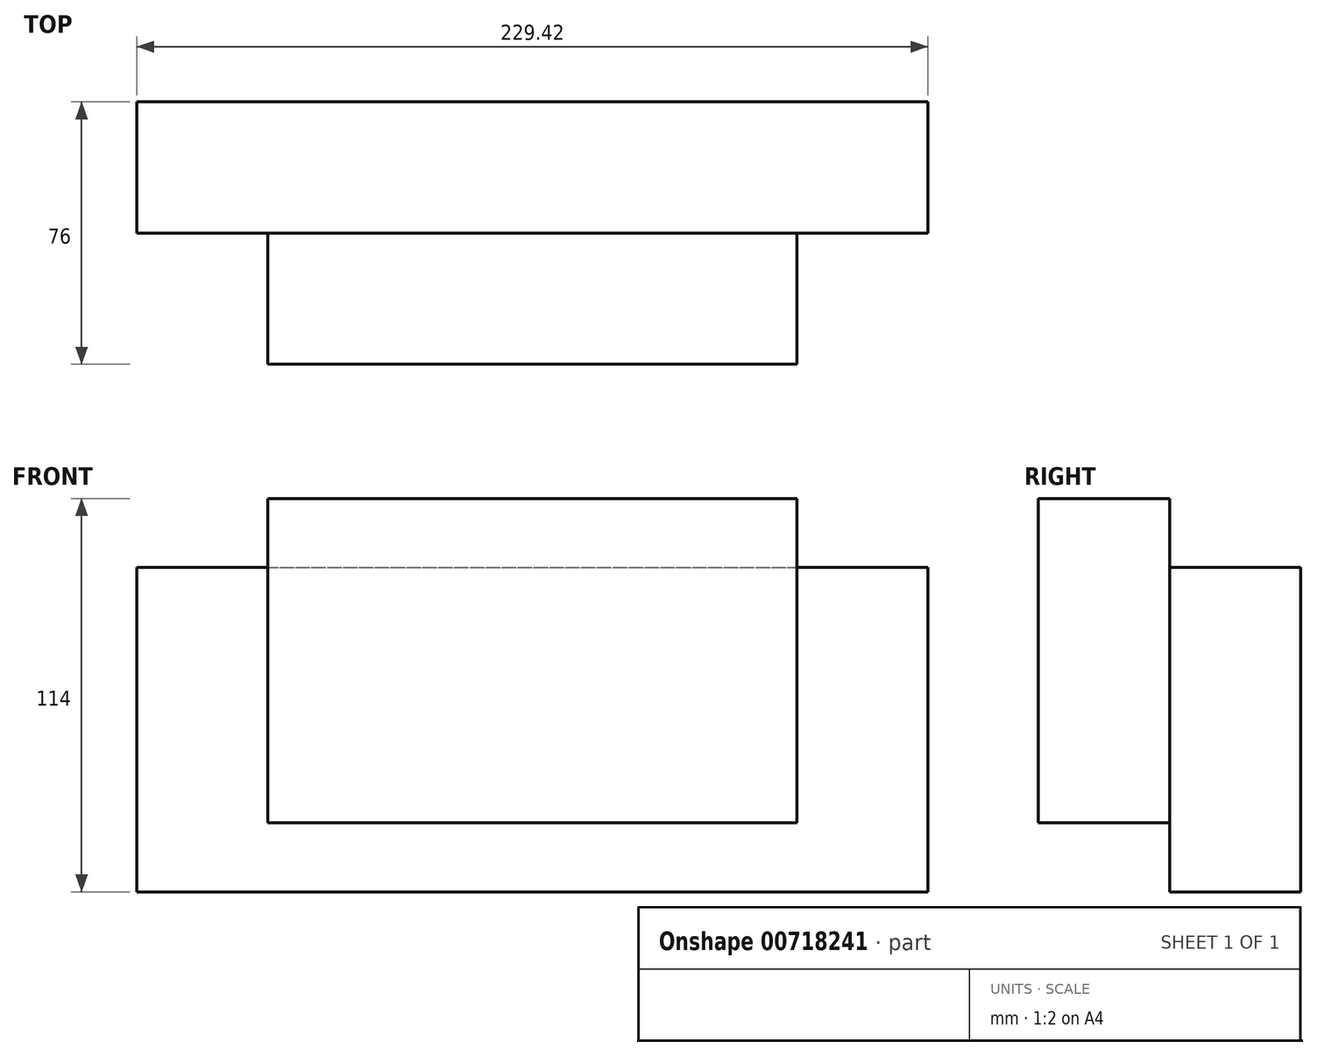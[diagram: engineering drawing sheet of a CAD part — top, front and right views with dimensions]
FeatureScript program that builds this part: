
annotation { "Feature Type Name" : "Feature", "Feature Type Description" : "" }
export const myFeature = defineFeature(function(context is Context, id is Id, definition is map)
    precondition{}
    {
        {
            var Q0;
            Q0=qCreatedBy(makeId("Front.planeOp"),FACE);
            var sketch = newSketch(context, id + "F0", { "sketchPlane" : qUnion([Q0])});
            skLineSegment(sketch, "E0.bottom", {"start": v(114.71, -57) * mm, "end": v(-114.71, -57) * mm});
            skLineSegment(sketch, "E0.top", {"start": v(114.71, 57) * mm, "end": v(-114.71, 57) * mm});
            skLineSegment(sketch, "E0.left", {"start": v(114.71, -57) * mm, "end": v(114.71, 57) * mm});
            skLineSegment(sketch, "E0.right", {"start": v(-114.71, -57) * mm, "end": v(-114.71, 57) * mm});
            skPoint(sketch, "E0.middle", {"position": v(0, 0) * mm});
            skSolve(sketch);
        }
        {
            var Q0;
            Q0=makeQuery(id+"F0.imprint","IMPRINT",FACE,{"disambiguationData":[TD([[makeQuery(id+"F0.imprint","IMPRINT",EDGE,{"derivedFrom":sQuery(id+"F0.wireOp",EDGE,"E0.bottom")}),-1.0]])]});
            extrude(context, id + "F1", {"entities" : qUnion([Q0]), "depth" : 76 * mm, "offsetDistance" : 25 * mm});
        }
        {
            var Q0;
            Q0=qCreatedBy(makeId("Right.planeOp"),FACE);
            cPlane(context, id + "F2", {"entities" : qUnion([Q0]), "cplaneType" : CPlaneType.OFFSET, "offset" : 115 * mm, "width" : 150 * mm, "height" : 150 * mm});
        }
        {
            var Q0;
            Q0=qCreatedBy(id+"F2.planeOp",FACE);
            var sketch = newSketch(context, id + "F3", { "sketchPlane" : qUnion([Q0])});
            skLineSegment(sketch, "E1.bottom", {"start": v(0, 57) * mm, "end": v(-38, 57) * mm});
            skLineSegment(sketch, "E1.top", {"start": v(0, 37) * mm, "end": v(-38, 37) * mm});
            skLineSegment(sketch, "E1.left", {"start": v(0, 57) * mm, "end": v(0, 37) * mm});
            skLineSegment(sketch, "E1.right", {"start": v(-38, 57) * mm, "end": v(-38, 37) * mm});
            skLineSegment(sketch, "E2.bottom", {"start": v(-76, -37) * mm, "end": v(-38, -37) * mm});
            skLineSegment(sketch, "E2.top", {"start": v(-76, -57) * mm, "end": v(-38, -57) * mm});
            skLineSegment(sketch, "E2.left", {"start": v(-76, -37) * mm, "end": v(-76, -57) * mm});
            skLineSegment(sketch, "E2.right", {"start": v(-38, -37) * mm, "end": v(-38, -57) * mm});
            skSolve(sketch);
        }
        {
            var Q0;
            Q0=makeQuery(id+"F3.imprint","IMPRINT",FACE,{"disambiguationData":[TD([[makeQuery(id+"F3.imprint","IMPRINT",EDGE,{"derivedFrom":sQuery(id+"F3.wireOp",EDGE,"E1.bottom")}),1.0]])]});
            var Q1;
            Q1=makeQuery(id+"F3.imprint","IMPRINT",FACE,{"disambiguationData":[TD([[makeQuery(id+"F3.imprint","IMPRINT",EDGE,{"derivedFrom":sQuery(id+"F3.wireOp",EDGE,"E2.bottom")}),-1.0]])]});
            extrude(context, id + "F4", {"entities" : qUnion([Q0, Q1]), "operationType" : NewBodyOperationType.REMOVE, "endBound" : BoundingType.THROUGH_ALL, "oppositeDirection" : true, "depth" : 25 * mm, "offsetDistance" : 25 * mm});
        }
        {
            var Q0;
            Q0=qCreatedBy(makeId("Top.planeOp"),FACE);
            cPlane(context, id + "F5", {"entities" : qUnion([Q0]), "cplaneType" : CPlaneType.OFFSET, "offset" : 57 * mm, "width" : 150 * mm, "height" : 150 * mm});
        }
        {
            var Q0;
            Q0=qCreatedBy(id+"F5.planeOp",FACE);
            var sketch = newSketch(context, id + "F6", { "sketchPlane" : qUnion([Q0])});
            skLineSegment(sketch, "E3.bottom", {"start": v(-114.71, -76) * mm, "end": v(-76.71, -76) * mm});
            skLineSegment(sketch, "E3.top", {"start": v(-114.71, -38) * mm, "end": v(-76.71, -38) * mm});
            skLineSegment(sketch, "E3.left", {"start": v(-114.71, -76) * mm, "end": v(-114.71, -38) * mm});
            skLineSegment(sketch, "E3.right", {"start": v(-76.71, -76) * mm, "end": v(-76.71, -38) * mm});
            skLineSegment(sketch, "E4.bottom", {"start": v(114.71, -76) * mm, "end": v(76.71, -76) * mm});
            skLineSegment(sketch, "E4.top", {"start": v(114.71, -38) * mm, "end": v(76.71, -38) * mm});
            skLineSegment(sketch, "E4.left", {"start": v(114.71, -76) * mm, "end": v(114.71, -38) * mm});
            skLineSegment(sketch, "E4.right", {"start": v(76.71, -76) * mm, "end": v(76.71, -38) * mm});
            skSolve(sketch);
        }
        {
            var Q0;
            Q0=makeQuery(id+"F6.imprint","IMPRINT",FACE,{"disambiguationData":[TD([[makeQuery(id+"F6.imprint","IMPRINT",EDGE,{"derivedFrom":sQuery(id+"F6.wireOp",EDGE,"E3.bottom")}),1.0]])]});
            var Q1;
            Q1=makeQuery(id+"F6.imprint","IMPRINT",FACE,{"disambiguationData":[TD([[makeQuery(id+"F6.imprint","IMPRINT",EDGE,{"derivedFrom":sQuery(id+"F6.wireOp",EDGE,"E4.bottom")}),-1.0]])]});
            extrude(context, id + "F7", {"entities" : qUnion([Q0, Q1]), "operationType" : NewBodyOperationType.REMOVE, "endBound" : BoundingType.THROUGH_ALL, "oppositeDirection" : true, "depth" : 25 * mm, "offsetDistance" : 25 * mm});
        }
    });
